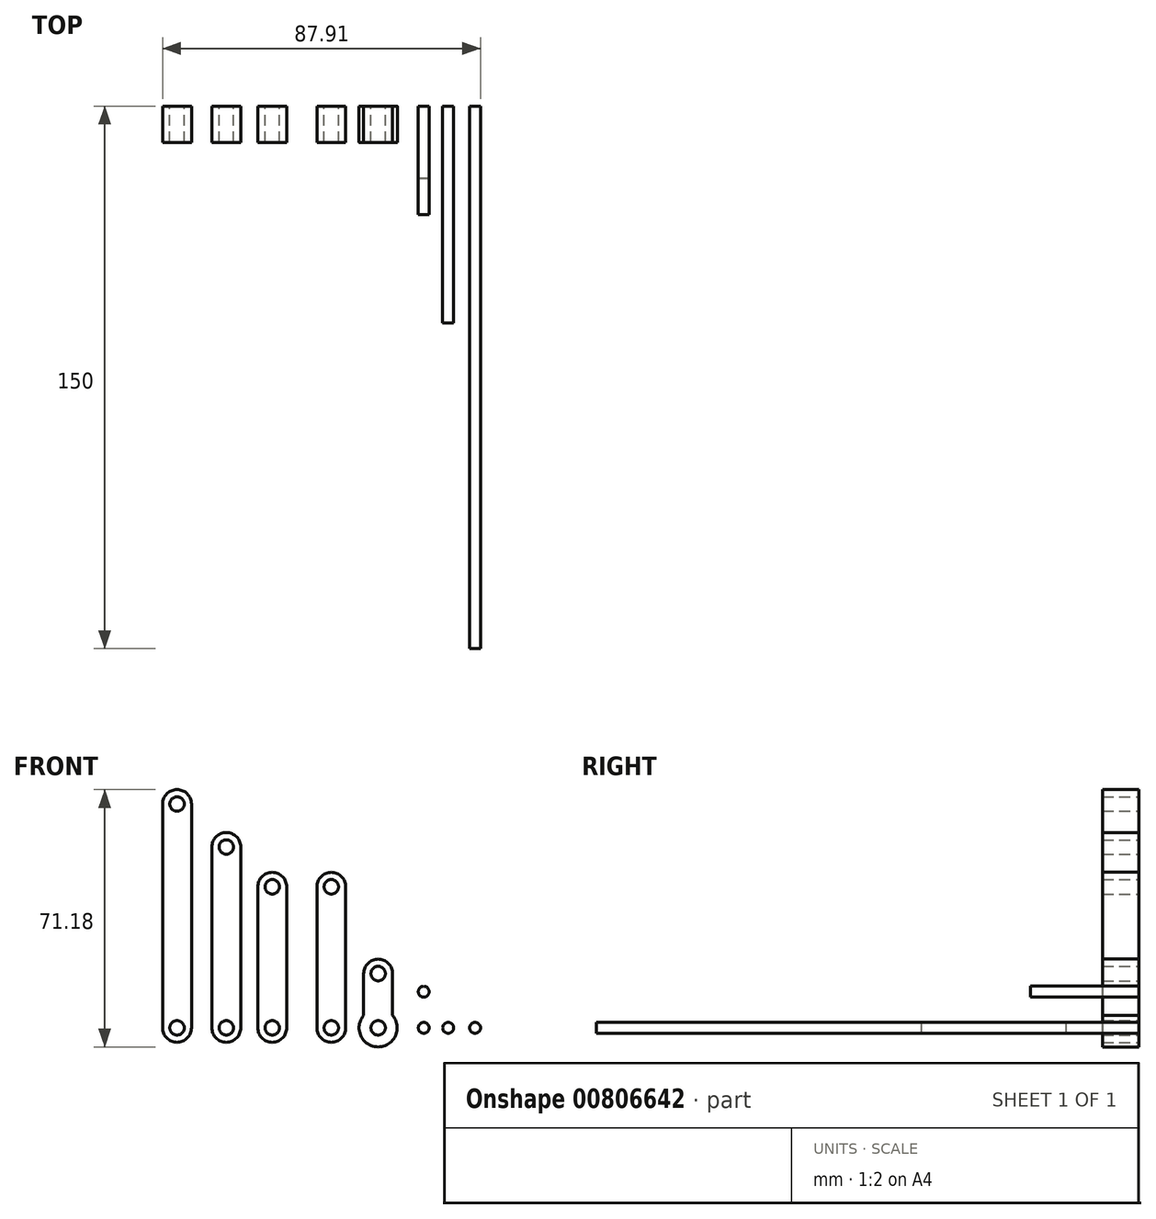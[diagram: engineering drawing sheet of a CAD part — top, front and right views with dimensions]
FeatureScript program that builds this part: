
annotation { "Feature Type Name" : "Feature", "Feature Type Description" : "" }
export const myFeature = defineFeature(function(context is Context, id is Id, definition is map)
    precondition{}
    {
        {
            assignVariable(context, id + "F0", {"name" : "thinkness", "anyValue" : 10});
        }
        {
            var Q0;
            Q0=qCreatedBy(makeId("Front.planeOp"),FACE);
            var sketch = newSketch(context, id + "F1", { "sketchPlane" : qUnion([Q0])});
            skArc(sketch, "E0", {"start": v(-8.6, 15) * mm, "mid": v(-12.6, 19) * mm, "end": v(-16.6, 15) * mm});
            skLineSegment(sketch, "E1", {"start": v(-16.6, 15) * mm, "end": v(-16.6, 3.45) * mm});
            skLineSegment(sketch, "E2", {"start": v(-8.6, 3.45) * mm, "end": v(-8.6, 15) * mm});
            skCircle(sketch, "E3", {"center": v(-12.6, 15) * mm, "radius": 2 * mm});
            skCircle(sketch, "E4", {"center": v(-12.6, 0) * mm, "radius": 2 * mm});
            skArc(sketch, "E5", {"start": v(-16.6, 3.45) * mm, "mid": v(-12.6, -5.28) * mm, "end": v(-8.6, 3.45) * mm});
            skSolve(sketch);
        }
        {
            var Q0;
            Q0=makeQuery(id+"F1.imprint","IMPRINT",FACE,{"disambiguationData":[TD([[makeQuery(id+"F1.imprint","IMPRINT",EDGE,{"derivedFrom":sQuery(id+"F1.wireOp",EDGE,"7ziRHkNs-eO90-hHvI-gxLj-cSdmEfLFaYHR")}),1.0]])]});
            var Q1;
            Q1=makeQuery(id+"F1.imprint","IMPRINT",FACE,{"disambiguationData":[TD([[makeQuery(id+"F1.imprint","IMPRINT",EDGE,{"derivedFrom":sQuery(id+"F1.wireOp",EDGE,"E0")}),1.0]])]});
            extrude(context, id + "F2", {"entities" : qUnion([Q0, Q1]), "depth" : (getVariable(context, 'thinkness')) * mm, "offsetDistance" : 25 * mm});
        }
        {
            var Q0;
            Q0=qCreatedBy(makeId("Front.planeOp"),FACE);
            var sketch = newSketch(context, id + "F3", { "sketchPlane" : qUnion([Q0])});
            skArc(sketch, "E6", {"start": v(-29.54, 0) * mm, "mid": v(-25.54, -4) * mm, "end": v(-21.54, 0) * mm});
            skArc(sketch, "E7", {"start": v(-21.54, 39) * mm, "mid": v(-25.54, 43) * mm, "end": v(-29.54, 39) * mm});
            skLineSegment(sketch, "E8", {"start": v(-29.54, 39) * mm, "end": v(-29.54, 0) * mm});
            skLineSegment(sketch, "E9", {"start": v(-21.54, 0) * mm, "end": v(-21.54, 39) * mm});
            skCircle(sketch, "E10", {"center": v(-25.54, 39) * mm, "radius": 2 * mm});
            skCircle(sketch, "E11", {"center": v(-25.54, 0) * mm, "radius": 2 * mm});
            skSolve(sketch);
        }
        {
            var Q0;
            Q0=makeQuery(id+"F3.imprint","IMPRINT",FACE,{"disambiguationData":[TD([[makeQuery(id+"F3.imprint","IMPRINT",EDGE,{"derivedFrom":sQuery(id+"F3.wireOp",EDGE,"E6")}),1.0]])]});
            extrude(context, id + "F4", {"entities" : qUnion([Q0]), "depth" : (getVariable(context, 'thinkness')) * mm, "offsetDistance" : 25 * mm});
        }
        {
            var Q0;
            Q0=qCreatedBy(makeId("Front.planeOp"),FACE);
            var sketch = newSketch(context, id + "F5", { "sketchPlane" : qUnion([Q0])});
            skArc(sketch, "E12", {"start": v(-45.88, 0) * mm, "mid": v(-41.88, -4) * mm, "end": v(-37.88, 0) * mm});
            skArc(sketch, "E13", {"start": v(-37.88, 39) * mm, "mid": v(-41.88, 43) * mm, "end": v(-45.88, 39) * mm});
            skLineSegment(sketch, "E14", {"start": v(-45.88, 39) * mm, "end": v(-45.88, 0) * mm});
            skLineSegment(sketch, "E15", {"start": v(-37.88, 0) * mm, "end": v(-37.88, 39) * mm});
            skCircle(sketch, "E16", {"center": v(-41.88, 39) * mm, "radius": 2 * mm});
            skCircle(sketch, "E17", {"center": v(-41.88, 0) * mm, "radius": 2 * mm});
            skSolve(sketch);
        }
        {
            var Q0;
            Q0=makeQuery(id+"F5.imprint","IMPRINT",FACE,{"disambiguationData":[TD([[makeQuery(id+"F5.imprint","IMPRINT",EDGE,{"derivedFrom":sQuery(id+"F5.wireOp",EDGE,"E12")}),1.0]])]});
            extrude(context, id + "F6", {"entities" : qUnion([Q0]), "depth" : (getVariable(context, 'thinkness')) * mm, "offsetDistance" : 25 * mm});
        }
        {
            var Q0;
            Q0=qCreatedBy(makeId("Front.planeOp"),FACE);
            var sketch = newSketch(context, id + "F7", { "sketchPlane" : qUnion([Q0])});
            skArc(sketch, "E18", {"start": v(-58.57, 0) * mm, "mid": v(-54.57, -4) * mm, "end": v(-50.57, 0) * mm});
            skArc(sketch, "E19", {"start": v(-50.57, 50) * mm, "mid": v(-54.57, 54) * mm, "end": v(-58.57, 50) * mm});
            skLineSegment(sketch, "E20", {"start": v(-58.57, 50) * mm, "end": v(-58.57, 0) * mm});
            skLineSegment(sketch, "E21", {"start": v(-50.57, 0) * mm, "end": v(-50.57, 50) * mm});
            skCircle(sketch, "E22", {"center": v(-54.57, 50) * mm, "radius": 2 * mm});
            skCircle(sketch, "E23", {"center": v(-54.57, 0) * mm, "radius": 2 * mm});
            skSolve(sketch);
        }
        {
            var Q0;
            Q0=makeQuery(id+"F7.imprint","IMPRINT",FACE,{"disambiguationData":[TD([[makeQuery(id+"F7.imprint","IMPRINT",EDGE,{"derivedFrom":sQuery(id+"F7.wireOp",EDGE,"E18")}),1.0]])]});
            extrude(context, id + "F8", {"entities" : qUnion([Q0]), "depth" : (getVariable(context, 'thinkness')) * mm, "offsetDistance" : 25 * mm});
        }
        {
            var Q0;
            Q0=qCreatedBy(makeId("Front.planeOp"),FACE);
            var sketch = newSketch(context, id + "F9", { "sketchPlane" : qUnion([Q0])});
            skArc(sketch, "E24", {"start": v(-72.2, 0) * mm, "mid": v(-68.2, -4) * mm, "end": v(-64.2, 0) * mm});
            skArc(sketch, "E25", {"start": v(-64.2, 61.9) * mm, "mid": v(-68.2, 65.9) * mm, "end": v(-72.2, 61.9) * mm});
            skLineSegment(sketch, "E26", {"start": v(-72.2, 61.9) * mm, "end": v(-72.2, 0) * mm});
            skLineSegment(sketch, "E27", {"start": v(-64.2, 0) * mm, "end": v(-64.2, 61.9) * mm});
            skCircle(sketch, "E28", {"center": v(-68.2, 61.9) * mm, "radius": 2 * mm});
            skCircle(sketch, "E29", {"center": v(-68.2, 0) * mm, "radius": 2 * mm});
            skSolve(sketch);
        }
        {
            var Q0;
            Q0=makeQuery(id+"F9.imprint","IMPRINT",FACE,{"disambiguationData":[TD([[makeQuery(id+"F9.imprint","IMPRINT",EDGE,{"derivedFrom":sQuery(id+"F9.wireOp",EDGE,"E24")}),1.0]])]});
            extrude(context, id + "F10", {"entities" : qUnion([Q0]), "depth" : (getVariable(context, 'thinkness')) * mm, "offsetDistance" : 25 * mm});
        }
        {
            var Q0;
            Q0=qCreatedBy(makeId("Front.planeOp"),FACE);
            var sketch = newSketch(context, id + "F11", { "sketchPlane" : qUnion([Q0])});
            skCircle(sketch, "E30", {"center": v(0, 0) * mm, "radius": 1.5 * mm});
            skSolve(sketch);
        }
        {
            var Q0;
            Q0=qSketchRegion(id+"F11",true);
            extrude(context, id + "F12", {"entities" : qUnion([Q0]), "depth" : (getVariable(context, 'thinkness') * 2) * mm, "offsetDistance" : 25 * mm});
        }
        {
            var Q0;
            Q0=qCreatedBy(makeId("Front.planeOp"),FACE);
            var sketch = newSketch(context, id + "F13", { "sketchPlane" : qUnion([Q0])});
            skCircle(sketch, "E31", {"center": v(6.75, 0) * mm, "radius": 1.5 * mm});
            skCircle(sketch, "E32", {"center": v(14.2, 0) * mm, "radius": 1.5 * mm});
            skSolve(sketch);
        }
        {
            var Q0;
            Q0=makeQuery(id+"F13.imprint","IMPRINT",FACE,{"disambiguationData":[TD([[makeQuery(id+"F13.imprint","IMPRINT",EDGE,{"derivedFrom":sQuery(id+"F13.wireOp",EDGE,"E31")}),1.0]])]});
            extrude(context, id + "F14", {"entities" : qUnion([Q0]), "depth" : (getVariable(context, 'thinkness') * 6) * mm, "offsetDistance" : 25 * mm});
        }
        {
            var Q0;
            Q0=makeQuery(id+"F13.imprint","IMPRINT",FACE,{"disambiguationData":[TD([[makeQuery(id+"F13.imprint","IMPRINT",EDGE,{"derivedFrom":sQuery(id+"F13.wireOp",EDGE,"E32")}),1.0]])]});
            extrude(context, id + "F15", {"entities" : qUnion([Q0]), "depth" : 150 * mm, "offsetDistance" : 25 * mm});
        }
        {
            var Q0;
            Q0=qCreatedBy(makeId("Front.planeOp"),FACE);
            var sketch = newSketch(context, id + "F16", { "sketchPlane" : qUnion([Q0])});
            skCircle(sketch, "E33", {"center": v(0, 10) * mm, "radius": 1.5 * mm});
            skSolve(sketch);
        }
        {
            var Q0;
            Q0=makeQuery(id+"F16.imprint","IMPRINT",FACE,{"disambiguationData":[TD([[makeQuery(id+"F16.imprint","IMPRINT",EDGE,{"derivedFrom":sQuery(id+"F16.wireOp",EDGE,"E33")}),1.0]])]});
            extrude(context, id + "F17", {"entities" : qUnion([Q0]), "depth" : (getVariable(context, 'thinkness') * 3) * mm, "offsetDistance" : 25 * mm});
        }
    });
